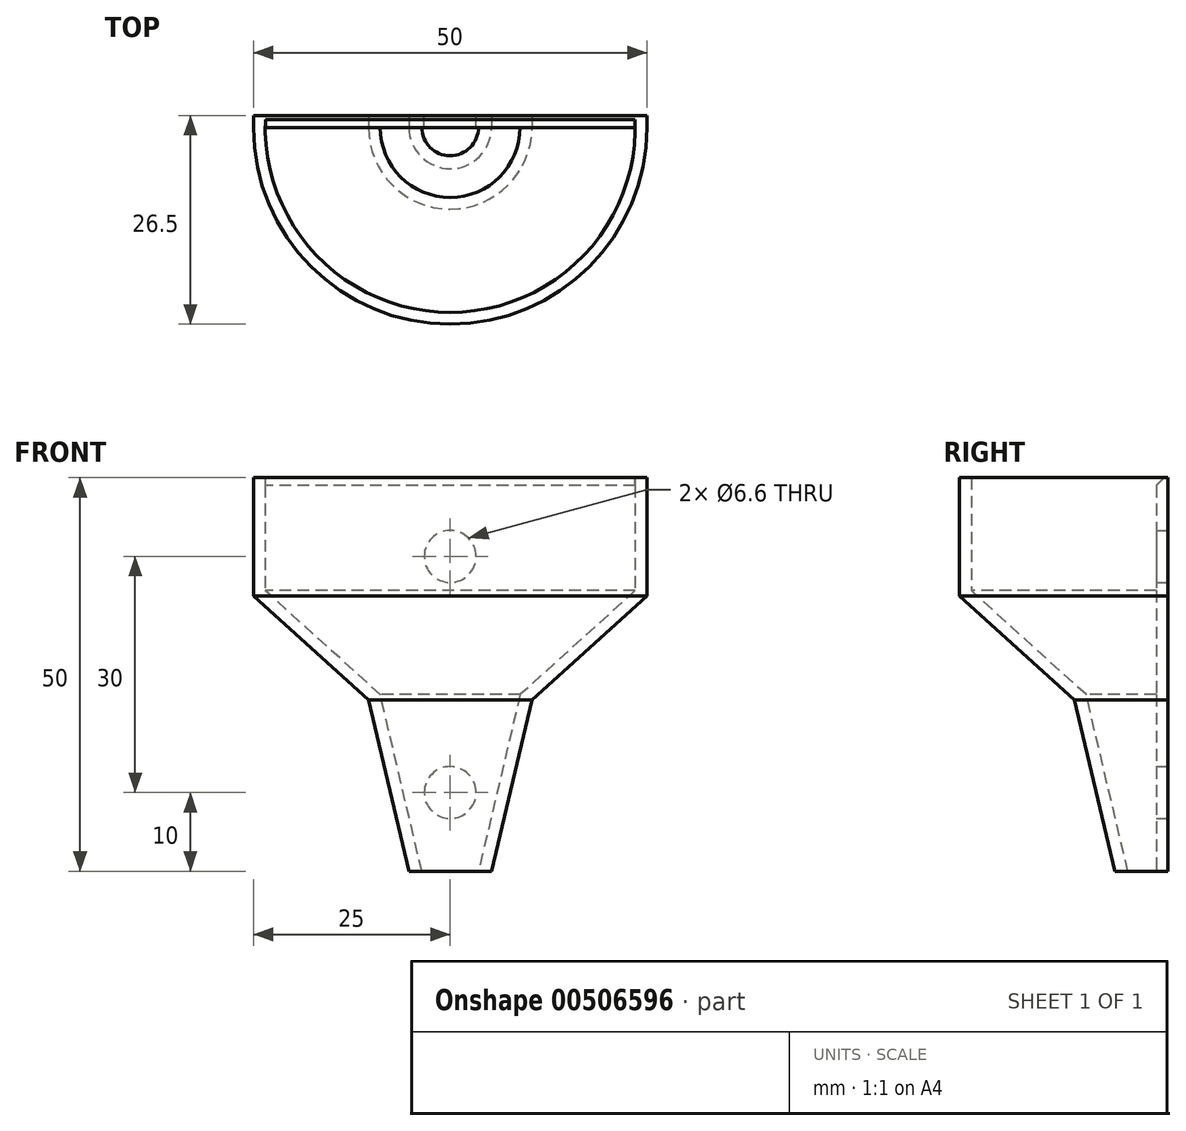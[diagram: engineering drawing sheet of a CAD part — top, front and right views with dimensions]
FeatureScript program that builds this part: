
annotation { "Feature Type Name" : "Feature", "Feature Type Description" : "" }
export const myFeature = defineFeature(function(context is Context, id is Id, definition is map)
    precondition{}
    {
        {
            var Q0;
            Q0=qCreatedBy(makeId("Front.planeOp"),FACE);
            var sketch = newSketch(context, id + "F0", { "sketchPlane" : qUnion([Q0])});
            skLineSegment(sketch, "E0", {"start": v(0, 0) * mm, "end": v(0, 64.33) * mm, "construction": true});
            skLineSegment(sketch, "E1", {"start": v(-23.5, 48.5) * mm, "end": v(-23.5, 35.67) * mm});
            skLineSegment(sketch, "E2", {"start": v(-23.5, 35.67) * mm, "end": v(-8.88, 22.44) * mm});
            skLineSegment(sketch, "E3.2", {"start": v(-25, 50) * mm, "end": v(-25, 35) * mm});
            skLineSegment(sketch, "E3.3", {"start": v(-25, 35) * mm, "end": v(-10.38, 21.78) * mm});
            skLineSegment(sketch, "E4", {"start": v(-10.38, 21.78) * mm, "end": v(-5.25, 0) * mm});
            skLineSegment(sketch, "E5", {"start": v(-8.88, 22.44) * mm, "end": v(-3.6, 0) * mm});
            skLineSegment(sketch, "E6", {"start": v(-3.6, 0) * mm, "end": v(-5.25, 0) * mm});
            skLineSegment(sketch, "E7", {"start": v(-25, 50) * mm, "end": v(-23.5, 50) * mm});
            skLineSegment(sketch, "E8", {"start": v(-23.5, 50) * mm, "end": v(-23.5, 48.5) * mm});
            skSolve(sketch);
        }
        {
            var Q0;
            Q0 = qSketchRegion(id + "F0", true);
            var Q1;
            Q1=sQuery(id+"F0.wireOp",EDGE,"E0");
            revolve(context, id + "F1", {"entities" : qUnion([Q0]), "axis" : qUnion([Q1]), "revolveType" : RevolveType.FULL});
        }
        {
            var Q0;
            Q0=qCreatedBy(makeId("Top.planeOp"),FACE);
            var sketch = newSketch(context, id + "F2", { "sketchPlane" : qUnion([Q0])});
            skLineSegment(sketch, "E9.bottom", {"start": v(-31.15, 0) * mm, "end": v(49.04, 0) * mm});
            skLineSegment(sketch, "E9.top", {"start": v(-31.15, 33.56) * mm, "end": v(49.04, 33.56) * mm});
            skLineSegment(sketch, "E9.left", {"start": v(-31.15, 0) * mm, "end": v(-31.15, 33.56) * mm});
            skLineSegment(sketch, "E9.right", {"start": v(49.04, 0) * mm, "end": v(49.04, 33.56) * mm});
            skSolve(sketch);
        }
        {
            var Q0;
            Q0 = qSketchRegion(id + "F2", true);
            extrude(context, id + "F3", {"entities" : qUnion([Q0]), "operationType" : NewBodyOperationType.REMOVE, "depth" : 69.4 * mm});
        }
        {
            var Q0;
            Q0=makeQuery(id+"F3.boolean.opBoolean","COPY",FACE,{"disambiguationData":[OD(1.0)],"derivedFrom":makeQuery(id+"F3.opExtrude","SWEPT_FACE",FACE,{"disambiguationData":[OSD([sQuery(id+"F2.wireOp",EDGE,"E9.bottom")])]})});
            var sketch = newSketch(context, id + "F4", { "sketchPlane" : qUnion([Q0])});
            skLineSegment(sketch, "E10.0", {"start": v(-25, 50) * mm, "end": v(-25, 35) * mm});
            skLineSegment(sketch, "E10.1", {"start": v(-25, 35) * mm, "end": v(-10.38, 21.78) * mm});
            skLineSegment(sketch, "E10.2", {"start": v(-10.38, 21.78) * mm, "end": v(-5.25, 0) * mm});
            skLineSegment(sketch, "E10.3", {"start": v(5.25, 0) * mm, "end": v(10.38, 21.78) * mm});
            skLineSegment(sketch, "E10.4", {"start": v(10.38, 21.78) * mm, "end": v(25, 35) * mm});
            skLineSegment(sketch, "E10.5", {"start": v(25, 35) * mm, "end": v(25, 50) * mm});
            skLineSegment(sketch, "E11", {"start": v(-25, 50) * mm, "end": v(25, 50) * mm});
            skLineSegment(sketch, "E12", {"start": v(-5.25, 0) * mm, "end": v(5.25, 0) * mm});
            skSolve(sketch);
        }
        {
            var Q0;
            Q0 = qSketchRegion(id + "F4", true);
            extrude(context, id + "F5", {"entities" : qUnion([Q0]), "operationType" : NewBodyOperationType.ADD, "depth" : 1.5 * mm});
        }
        {
            var Q0;
            Q0=makeQuery(id+"F5.opExtrude","CAP_FACE",FACE,{"disambiguationData":[OSD([sQuery(id+"F4.wireOp",EDGE,"E10.0"),sQuery(id+"F4.wireOp",EDGE,"E10.1"),sQuery(id+"F4.wireOp",EDGE,"E10.2"),sQuery(id+"F4.wireOp",EDGE,"E10.3"),sQuery(id+"F4.wireOp",EDGE,"E10.4"),sQuery(id+"F4.wireOp",EDGE,"E10.5"),sQuery(id+"F4.wireOp",EDGE,"E11"),sQuery(id+"F4.wireOp",EDGE,"E12")])],"isStart":false});
            var sketch = newSketch(context, id + "F6", { "sketchPlane" : qUnion([Q0])});
            skLineSegment(sketch, "E13", {"start": v(0, -1.44) * mm, "end": v(0, 60.29) * mm, "construction": true});
            skPoint(sketch, "E13.startSnap0", {"position": v(0, 0) * mm});
            skPoint(sketch, "E13.endSnap0", {"position": v(0, 50) * mm});
            skCircle(sketch, "E14", {"center": v(0, 40) * mm, "radius": 3.3 * mm});
            skCircle(sketch, "E15", {"center": v(0, 10) * mm, "radius": 3.3 * mm});
            skSolve(sketch);
        }
        {
            var Q0;
            Q0 = qSketchRegion(id + "F6", true);
            extrude(context, id + "F7", {"entities" : qUnion([Q0]), "operationType" : NewBodyOperationType.REMOVE, "oppositeDirection" : true, "depth" : 3 * mm});
        }
        {
            var Q0;
            Q0=makeQuery(id+"F5.opExtrude","CAP_EDGE",EDGE,{"disambiguationData":[OSD([sQuery(id+"F4.wireOp",EDGE,"E11")])],"isStart":true});
            chamfer(context, id + "F8", {"entities" : qUnion([Q0]), "width" : 1 * mm, "tangentPropagation" : true});
        }
    });
